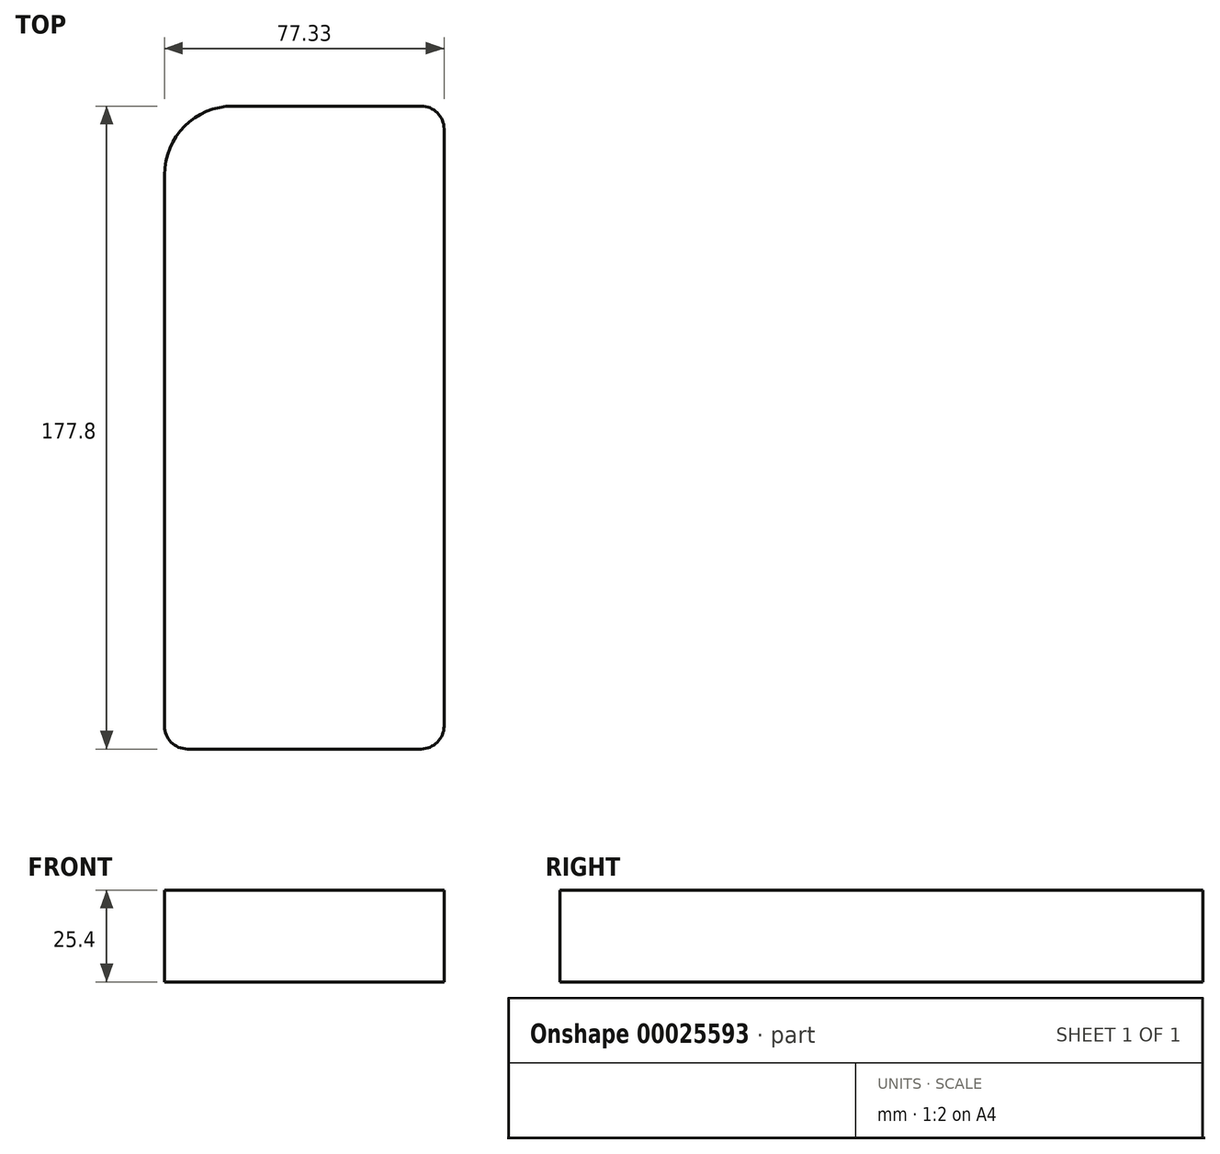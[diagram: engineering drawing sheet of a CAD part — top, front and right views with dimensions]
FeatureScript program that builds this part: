
annotation { "Feature Type Name" : "Feature", "Feature Type Description" : "" }
export const myFeature = defineFeature(function(context is Context, id is Id, definition is map)
    precondition{}
    {
        {
            var Q0;
            Q0=qCreatedBy(makeId("Top.planeOp"),FACE);
            var sketch = newSketch(context, id + "F0", { "sketchPlane" : qUnion([Q0])});
            skLineSegment(sketch, "E0.bottom", {"start": v(19.05, 102.1) * mm, "end": v(70.98, 102.1) * mm});
            skLineSegment(sketch, "E0.top", {"start": v(6.35, -75.7) * mm, "end": v(70.98, -75.7) * mm});
            skLineSegment(sketch, "E0.left", {"start": v(0, 83.05) * mm, "end": v(0, -69.35) * mm});
            skLineSegment(sketch, "E0.right", {"start": v(77.33, 95.75) * mm, "end": v(77.33, -69.35) * mm});
            skPoint(sketch, "E1.visualSharp", {"position": v(0, 102.1) * mm});
            skArc(sketch, "E1.filletArc", {"start": v(19.05, 102.1) * mm, "mid": v(5.58, 96.52) * mm, "end": v(0, 83.05) * mm});
            skPoint(sketch, "E2.visualSharp", {"position": v(77.33, -75.7) * mm});
            skArc(sketch, "E2.filletArc", {"start": v(70.98, -75.7) * mm, "mid": v(75.47, -73.84) * mm, "end": v(77.33, -69.35) * mm});
            skPoint(sketch, "E3.visualSharp", {"position": v(0, -75.7) * mm});
            skArc(sketch, "E3.filletArc", {"start": v(0, -69.35) * mm, "mid": v(1.86, -73.84) * mm, "end": v(6.35, -75.7) * mm});
            skPoint(sketch, "E4.visualSharp", {"position": v(77.33, 102.1) * mm});
            skArc(sketch, "E4.filletArc", {"start": v(77.33, 95.75) * mm, "mid": v(75.47, 100.24) * mm, "end": v(70.98, 102.1) * mm});
            skLineSegment(sketch, "E5", {"start": v(0, 0) * mm, "end": v(34.07, 0) * mm});
            skSolve(sketch);
        }
        {
            var Q0;
            Q0=makeQuery(id+"F0.imprint","IMPRINT",FACE,{"disambiguationData":[TD([[makeQuery(id+"F0.imprint","IMPRINT",EDGE,{"derivedFrom":sQuery(id+"F0.wireOp",EDGE,"E0.bottom")}),-1.0]])]});
            extrude(context, id + "F1", {"entities" : qUnion([Q0]), "depth" : 25.4 * mm});
        }
    });
